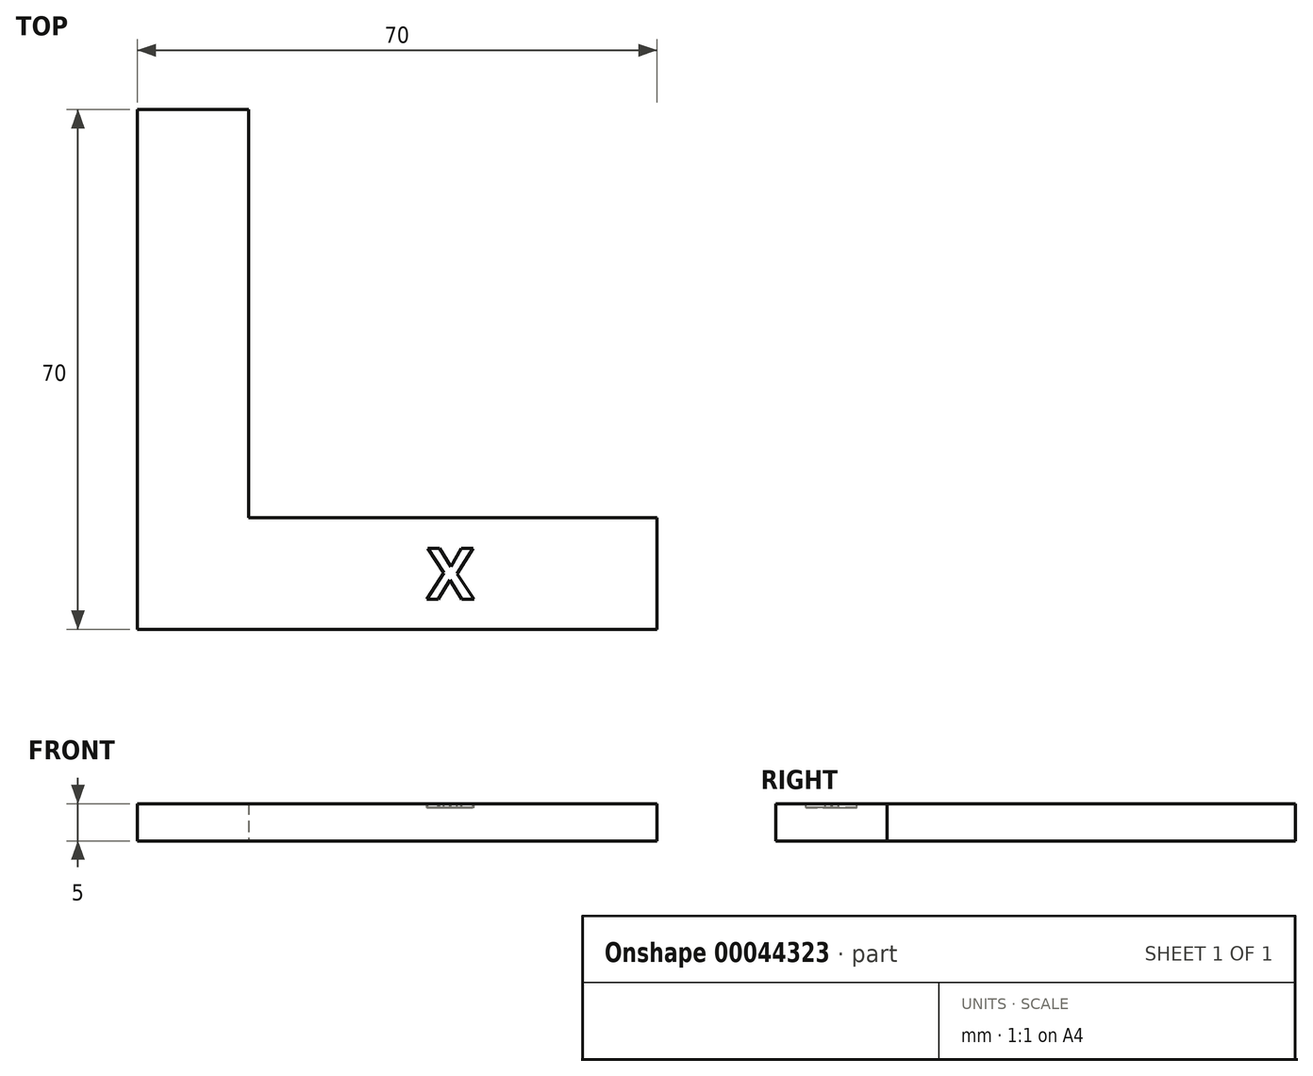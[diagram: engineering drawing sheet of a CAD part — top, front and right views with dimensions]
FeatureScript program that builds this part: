
annotation { "Feature Type Name" : "Feature", "Feature Type Description" : "" }
export const myFeature = defineFeature(function(context is Context, id is Id, definition is map)
    precondition{}
    {
        {
            var Q0;
            Q0=qCreatedBy(makeId("Top.planeOp"),FACE);
            var sketch = newSketch(context, id + "F0", { "sketchPlane" : qUnion([Q0])});
            skLineSegment(sketch, "E0", {"start": v(0, 55) * mm, "end": v(0, 0) * mm});
            skLineSegment(sketch, "E1", {"start": v(0, 0) * mm, "end": v(55, 0) * mm});
            skLineSegment(sketch, "E2", {"start": v(55, 0) * mm, "end": v(55, -15) * mm});
            skLineSegment(sketch, "E3", {"start": v(55, -15) * mm, "end": v(-15, -15) * mm});
            skLineSegment(sketch, "E4", {"start": v(-15, -15) * mm, "end": v(-15, 55) * mm});
            skLineSegment(sketch, "E5", {"start": v(-15, 55) * mm, "end": v(0, 55) * mm});
            skSolve(sketch);
        }
        {
            var Q0;
            Q0 = qSketchRegion(id + "F0", true);
            extrude(context, id + "F1", {"entities" : qUnion([Q0]), "depth" : 5 * mm});
        }
        {
            var Q0;
            Q0=makeQuery(id+"F1.opExtrude","CAP_FACE",FACE,{"disambiguationData":[OSD([sQuery(id+"F0.wireOp",EDGE,"E0"),sQuery(id+"F0.wireOp",EDGE,"E1"),sQuery(id+"F0.wireOp",EDGE,"E2"),sQuery(id+"F0.wireOp",EDGE,"E3"),sQuery(id+"F0.wireOp",EDGE,"E4"),sQuery(id+"F0.wireOp",EDGE,"E5")])],"isStart":false});
            var sketch = newSketch(context, id + "F2", { "sketchPlane" : qUnion([Q0])});
            skText(sketch, "E6", { "text": "X", "fontName": "OpenSans-Bold.ttf"});
            skPoint(sketch, "E7", {"position": v(27.5, -7.5) * mm});
            skPoint(sketch, "E8", {"position": v(55, -7.5) * mm});
            skPoint(sketch, "E9", {"position": v(27.5, 0) * mm});
            const initialGuessF2  = {"E6": [0.024, -0.01094, 1, 0, 0.00689]};
            skSetInitialGuess(sketch, initialGuessF2);
            skSolve(sketch);
        }
        {
            var Q0;
            Q0 = qSketchRegion(id + "F2", true);
            extrude(context, id + "F3", {"entities" : qUnion([Q0]), "operationType" : NewBodyOperationType.REMOVE, "oppositeDirection" : true, "depth" : 0.5 * mm});
        }
    });
